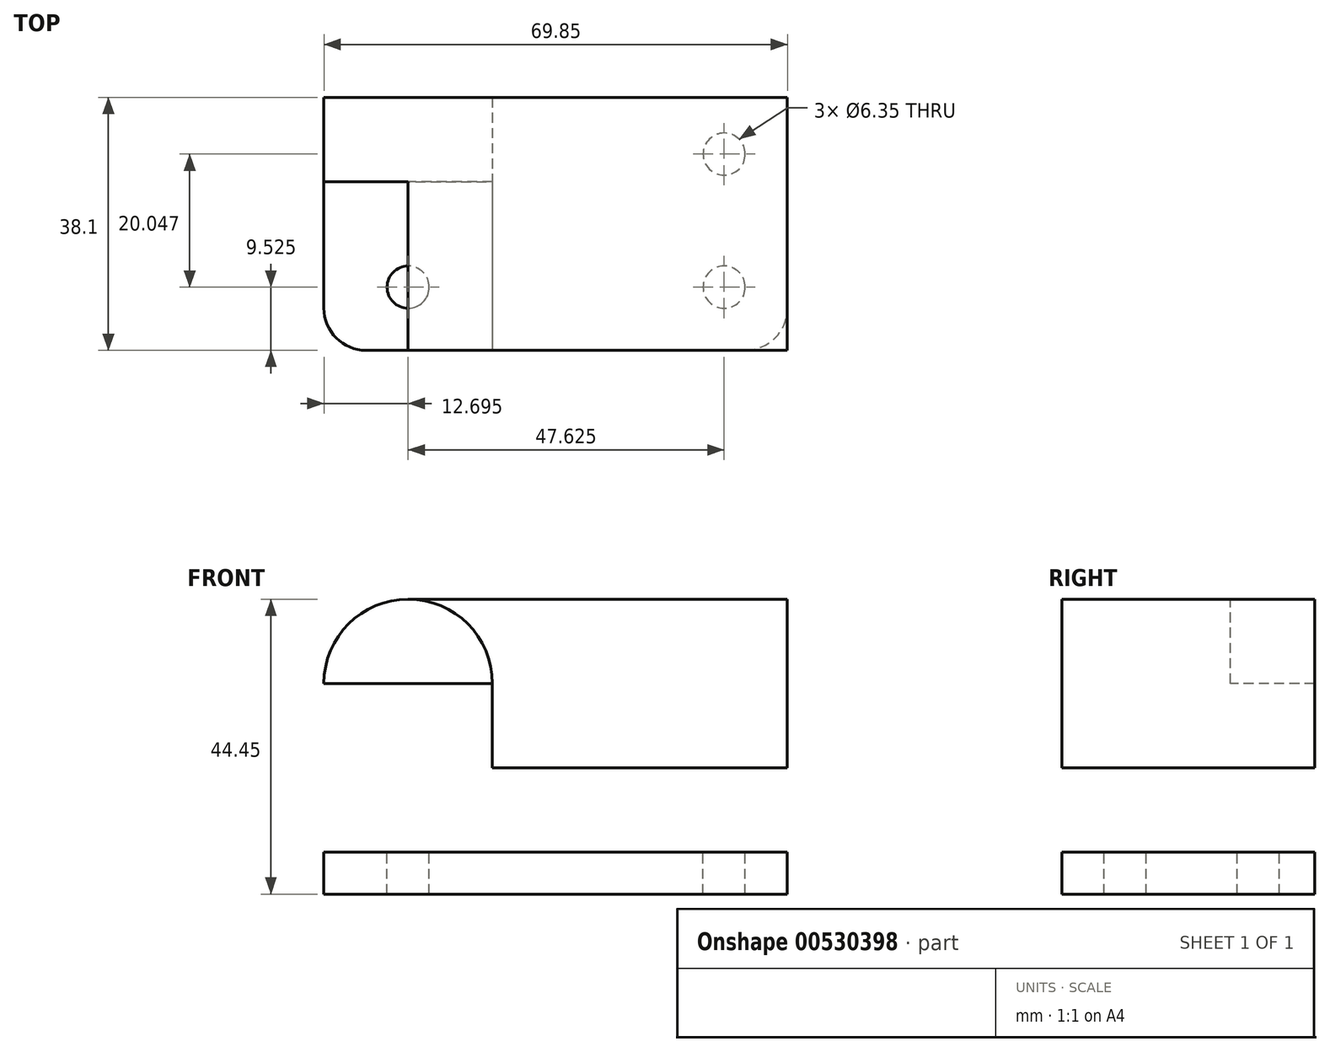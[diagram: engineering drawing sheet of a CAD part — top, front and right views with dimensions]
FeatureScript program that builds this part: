
annotation { "Feature Type Name" : "Feature", "Feature Type Description" : "" }
export const myFeature = defineFeature(function(context is Context, id is Id, definition is map)
    precondition{}
    {
        {
            var Q0;
            Q0=qCreatedBy(makeId("Front.planeOp"),FACE);
            var sketch = newSketch(context, id + "F0", { "sketchPlane" : qUnion([Q0])});
            skLineSegment(sketch, "E0", {"start": v(-49.33, 44.45) * mm, "end": v(-49.33, 0) * mm});
            skLineSegment(sketch, "E1", {"start": v(-49.33, 0) * mm, "end": v(20.52, 0) * mm});
            skLineSegment(sketch, "E2", {"start": v(20.52, 0) * mm, "end": v(20.52, 44.45) * mm});
            skLineSegment(sketch, "E3", {"start": v(-49.33, 44.45) * mm, "end": v(20.52, 44.45) * mm});
            skSolve(sketch);
        }
        {
            var Q0;
            Q0=makeQuery(id+"F0.imprint","IMPRINT",FACE,{"disambiguationData":[TD([[makeQuery(id+"F0.imprint","IMPRINT",EDGE,{"derivedFrom":sQuery(id+"F0.wireOp",EDGE,"E0")}),1.0]])]});
            extrude(context, id + "F1", {"entities" : qUnion([Q0]), "depth" : 38.1 * mm, "offsetDistance" : 25.4 * mm});
        }
        {
            var Q0;
            Q0=makeQuery(id+"F1.opExtrude","CAP_FACE",FACE,{"disambiguationData":[OSD([sQuery(id+"F0.wireOp",EDGE,"E0"),sQuery(id+"F0.wireOp",EDGE,"E1"),sQuery(id+"F0.wireOp",EDGE,"E2"),sQuery(id+"F0.wireOp",EDGE,"E3")])],"isStart":false});
            var sketch = newSketch(context, id + "F2", { "sketchPlane" : qUnion([Q0])});
            skLineSegment(sketch, "E4", {"start": v(-49.33, 0) * mm, "end": v(-49.33, 6.35) * mm});
            skLineSegment(sketch, "E5", {"start": v(-49.33, 6.35) * mm, "end": v(-23.93, 6.35) * mm});
            skLineSegment(sketch, "E6", {"start": v(-23.93, 6.35) * mm, "end": v(-23.93, 31.75) * mm});
            skLineSegment(sketch, "E7", {"start": v(-23.93, 31.75) * mm, "end": v(-49.33, 31.75) * mm});
            skLineSegment(sketch, "E8", {"start": v(-49.33, 31.75) * mm, "end": v(-49.33, 6.35) * mm});
            skLineSegment(sketch, "E9", {"start": v(-23.93, 6.35) * mm, "end": v(20.52, 6.35) * mm});
            skArc(sketch, "E10", {"start": v(-23.93, 31.75) * mm, "mid": v(-36.63, 44.45) * mm, "end": v(-49.33, 31.75) * mm});
            skLineSegment(sketch, "E11", {"start": v(-23.93, 31.75) * mm, "end": v(-23.93, 19.05) * mm});
            skLineSegment(sketch, "E12", {"start": v(-23.93, 19.05) * mm, "end": v(-23.93, 6.35) * mm});
            skLineSegment(sketch, "E13", {"start": v(-23.93, 19.05) * mm, "end": v(20.52, 19.05) * mm});
            skLineSegment(sketch, "E14", {"start": v(20.52, 19.05) * mm, "end": v(20.52, 6.35) * mm});
            skArc(sketch, "E15", {"start": v(-23.93, 19.05) * mm, "mid": v(-11.23, 6.35) * mm, "end": v(1.47, 19.05) * mm});
            skSolve(sketch);
        }
        {
            var Q0;
            {var subQ1=makeQuery(id+"F1.opExtrude","CAP_EDGE",EDGE,{"disambiguationData":[OSD([sQuery(id+"F0.wireOp",EDGE,"E0")])],"isStart":false});var subQ3=makeQuery(id+"F1.opExtrude","CAP_EDGE",EDGE,{"disambiguationData":[OSD([sQuery(id+"F0.wireOp",EDGE,"E3")])],"isStart":false});var subQ5=makeQuery(id+"F2.imprint","INTERSECT",VERTEX,{"derivedFrom":[subQ1,subQ3]});Q0=makeQuery(id+"F2.imprint","IMPRINT",FACE,{"disambiguationData":[TD([[makeQuery(id+"F2.imprint","IMPRINT",EDGE,{"disambiguationData":[TD([[subQ5,-1.0]])],"derivedFrom":subQ3}),-1.0]])]});}
            var Q1;
            {var subQ2=sQuery(id+"F2.wireOp",EDGE,"E11");Q1=makeQuery(id+"F2.imprint","IMPRINT",FACE,{"disambiguationData":[TD([[makeQuery(id+"F2.imprint","IMPRINT",EDGE,{"derivedFrom":subQ2}),1.0]])]});}
            var Q2;
            {var subQ0=sQuery(id+"F2.wireOp",EDGE,"E15");var subQ1=sQuery(id+"F2.wireOp",EDGE,"E13");var subQ3=makeQuery(id+"F2.imprint","INTERSECT",VERTEX,{"derivedFrom":[subQ1,subQ0]});Q2=makeQuery(id+"F2.imprint","IMPRINT",FACE,{"disambiguationData":[TD([[makeQuery(id+"F2.imprint","IMPRINT",EDGE,{"disambiguationData":[TD([[subQ3,1.0]])],"derivedFrom":subQ0}),1.0]])]});}
            var Q3;
            {var subQ0=sQuery(id+"F2.wireOp",EDGE,"E14");Q3=makeQuery(id+"F2.imprint","IMPRINT",FACE,{"disambiguationData":[TD([[makeQuery(id+"F2.imprint","IMPRINT",EDGE,{"derivedFrom":subQ0}),1.0]])]});}
            extrude(context, id + "F3", {"entities" : qUnion([Q0, Q1, Q2, Q3]), "operationType" : NewBodyOperationType.REMOVE, "endBound" : BoundingType.THROUGH_ALL, "oppositeDirection" : true, "depth" : 25.4 * mm, "offsetDistance" : 25.4 * mm});
        }
        {
            var Q0;
            Q0 = qSketchRegion(id + "F2", true);
            extrude(context, id + "F4", {"entities" : qUnion([Q0]), "operationType" : NewBodyOperationType.REMOVE, "oppositeDirection" : true, "depth" : 25.4 * mm, "offsetDistance" : 25.4 * mm});
        }
        {
            var Q0;
            {var subQ0=sQuery(id+"F2.wireOp",EDGE,"E9");Q0=makeQuery(id+"F4.boolean.opBoolean","MERGE",FACE,{"derivedFrom":[makeQuery(id+"F3.boolean.opBoolean","COPY",FACE,{"derivedFrom":makeQuery(id+"F3.opExtrude","SWEPT_FACE",FACE,{"disambiguationData":[OSD([subQ0])]})})],"fromTools":[makeQuery(id+"F4.opExtrude","SWEPT_FACE",FACE,{"disambiguationData":[OSD([sQuery(id+"F2.wireOp",EDGE,"E5"),subQ0])]})]});}
            var sketch = newSketch(context, id + "F5", { "sketchPlane" : qUnion([Q0])});
            skLineSegment(sketch, "E16", {"start": v(-49.33, -12.7) * mm, "end": v(-49.33, -31.75) * mm});
            skLineSegment(sketch, "E17", {"start": v(-49.33, -31.75) * mm, "end": v(-49.33, -38.1) * mm});
            skLineSegment(sketch, "E18", {"start": v(-49.33, -38.1) * mm, "end": v(-42.98, -38.1) * mm});
            skLineSegment(sketch, "E19", {"start": v(-42.98, -38.1) * mm, "end": v(-42.98, -31.75) * mm});
            skLineSegment(sketch, "E20", {"start": v(-42.98, -31.75) * mm, "end": v(-49.33, -31.75) * mm});
            skLineSegment(sketch, "E21", {"start": v(14.17, -38.1) * mm, "end": v(14.17, -31.75) * mm});
            skLineSegment(sketch, "E22", {"start": v(14.17, -31.75) * mm, "end": v(20.52, -31.75) * mm});
            skLineSegment(sketch, "E23", {"start": v(20.52, -38.1) * mm, "end": v(20.52, -31.75) * mm});
            skLineSegment(sketch, "E24", {"start": v(20.52, -31.75) * mm, "end": v(20.52, 0) * mm});
            skLineSegment(sketch, "E25", {"start": v(14.17, -38.1) * mm, "end": v(20.52, -38.1) * mm});
            skLineSegment(sketch, "E26", {"start": v(20.52, 0) * mm, "end": v(20.52, -31.75) * mm});
            skArc(sketch, "E27", {"start": v(14.17, -38.1) * mm, "mid": v(18.66, -36.24) * mm, "end": v(20.52, -31.75) * mm});
            skArc(sketch, "E28", {"start": v(-49.33, -31.75) * mm, "mid": v(-47.47, -36.24) * mm, "end": v(-42.98, -38.1) * mm});
            skCircle(sketch, "E29", {"center": v(11, -8.53) * mm, "radius": 3.18 * mm});
            skCircle(sketch, "E30", {"center": v(-36.63, -28.57) * mm, "radius": 3.18 * mm});
            skCircle(sketch, "E31", {"center": v(11, -28.57) * mm, "radius": 3.18 * mm});
            skSolve(sketch);
        }
        {
            var Q0;
            Q0=makeQuery(id+"F5.imprint","IMPRINT",FACE,{"disambiguationData":[TD([[makeQuery(id+"F5.imprint","IMPRINT",EDGE,{"derivedFrom":sQuery(id+"F5.wireOp",EDGE,"E29")}),1.0]])]});
            var Q1;
            Q1=makeQuery(id+"F5.imprint","IMPRINT",FACE,{"disambiguationData":[TD([[makeQuery(id+"F5.imprint","IMPRINT",EDGE,{"derivedFrom":sQuery(id+"F5.wireOp",EDGE,"E31")}),1.0]])]});
            var Q2;
            Q2=makeQuery(id+"F5.imprint","IMPRINT",FACE,{"disambiguationData":[TD([[makeQuery(id+"F5.imprint","IMPRINT",EDGE,{"derivedFrom":sQuery(id+"F5.wireOp",EDGE,"E17")}),1.0]])]});
            var Q3;
            Q3=makeQuery(id+"F5.imprint","IMPRINT",FACE,{"disambiguationData":[TD([[makeQuery(id+"F5.imprint","IMPRINT",EDGE,{"derivedFrom":sQuery(id+"F5.wireOp",EDGE,"E23")}),-1.0]])]});
            var Q4;
            Q4=makeQuery(id+"F5.imprint","IMPRINT",FACE,{"disambiguationData":[TD([[makeQuery(id+"F5.imprint","IMPRINT",EDGE,{"derivedFrom":sQuery(id+"F5.wireOp",EDGE,"E30")}),1.0]])]});
            extrude(context, id + "F6", {"entities" : qUnion([Q0, Q1, Q2, Q3, Q4]), "operationType" : NewBodyOperationType.REMOVE, "endBound" : BoundingType.THROUGH_ALL, "oppositeDirection" : true, "depth" : 25.4 * mm, "offsetDistance" : 25.4 * mm});
        }
        {
            var Q0;
            Q0=makeQuery(id+"F4.boolean.opBoolean","COPY",FACE,{"derivedFrom":makeQuery(id+"F4.opExtrude","CAP_FACE",FACE,{"disambiguationData":[OSD([sQuery(id+"F2.wireOp",EDGE,"E5"),sQuery(id+"F2.wireOp",EDGE,"E8"),sQuery(id+"F2.wireOp",EDGE,"E9"),sQuery(id+"F2.wireOp",EDGE,"E10"),sQuery(id+"F2.wireOp",EDGE,"E11"),sQuery(id+"F2.wireOp",EDGE,"E13"),sQuery(id+"F2.wireOp",EDGE,"E14")])],"isStart":false})});
            var sketch = newSketch(context, id + "F7", { "sketchPlane" : qUnion([Q0])});
            skLineSegment(sketch, "E32", {"start": v(-36.63, 44.45) * mm, "end": v(-36.63, 6.35) * mm});
            skLineSegment(sketch, "E33", {"start": v(-49.33, 31.75) * mm, "end": v(-23.93, 31.75) * mm});
            skCircle(sketch, "E34", {"center": v(-36.63, 31.75) * mm, "radius": 6.35 * mm});
            skSolve(sketch);
        }
        {
            var Q0;
            {var subQ0=sQuery(id+"F7.wireOp",EDGE,"E34");var subQ1=sQuery(id+"F7.wireOp",EDGE,"E32");var subQ2=makeQuery(id+"F7.imprint","INTERSECT",VERTEX,{"disambiguationData":[OD(0.0)],"derivedFrom":[subQ1,subQ0]});Q0=makeQuery(id+"F7.imprint","IMPRINT",FACE,{"disambiguationData":[TD([[makeQuery(id+"F7.imprint","IMPRINT",EDGE,{"disambiguationData":[TD([[subQ2,-1.0]])],"derivedFrom":subQ1}),-1.0]])]});}
            var Q1;
            {var subQ0=sQuery(id+"F7.wireOp",EDGE,"E34");var subQ1=sQuery(id+"F7.wireOp",EDGE,"E32");var subQ2=makeQuery(id+"F7.imprint","INTERSECT",VERTEX,{"disambiguationData":[OD(0.0)],"derivedFrom":[subQ1,subQ0]});Q1=makeQuery(id+"F7.imprint","IMPRINT",FACE,{"disambiguationData":[TD([[makeQuery(id+"F7.imprint","IMPRINT",EDGE,{"disambiguationData":[TD([[subQ2,-1.0]])],"derivedFrom":subQ1}),1.0]])]});}
            var Q2;
            {var subQ0=sQuery(id+"F7.wireOp",EDGE,"E33");var subQ1=sQuery(id+"F7.wireOp",EDGE,"E32");var subQ2=makeQuery(id+"F7.imprint","INTERSECT",VERTEX,{"derivedFrom":[subQ1,subQ0]});Q2=makeQuery(id+"F7.imprint","IMPRINT",FACE,{"disambiguationData":[TD([[makeQuery(id+"F7.imprint","IMPRINT",EDGE,{"disambiguationData":[TD([[subQ2,-1.0]])],"derivedFrom":subQ1}),1.0]])]});}
            var Q3;
            {var subQ0=sQuery(id+"F7.wireOp",EDGE,"E33");var subQ1=sQuery(id+"F7.wireOp",EDGE,"E32");var subQ2=makeQuery(id+"F7.imprint","INTERSECT",VERTEX,{"derivedFrom":[subQ1,subQ0]});Q3=makeQuery(id+"F7.imprint","IMPRINT",FACE,{"disambiguationData":[TD([[makeQuery(id+"F7.imprint","IMPRINT",EDGE,{"disambiguationData":[TD([[subQ2,-1.0]])],"derivedFrom":subQ1}),-1.0]])]});}
            extrude(context, id + "F8", {"entities" : qUnion([Q0, Q1, Q2, Q3]), "operationType" : NewBodyOperationType.REMOVE, "endBound" : BoundingType.THROUGH_ALL, "oppositeDirection" : true, "depth" : 25.4 * mm, "offsetDistance" : 25.4 * mm});
        }
    });
